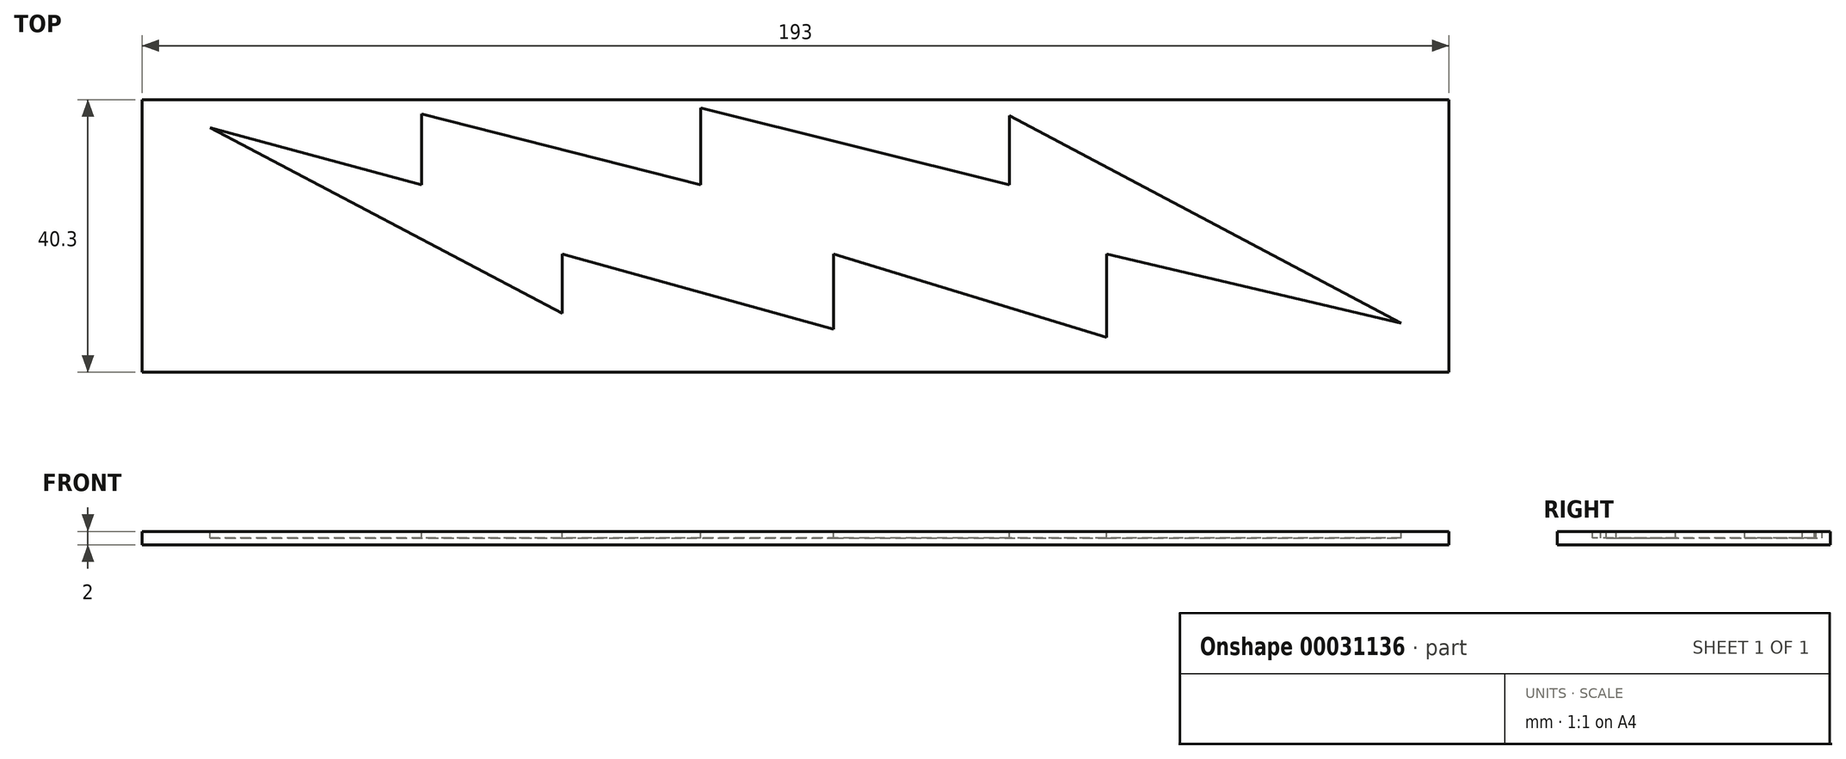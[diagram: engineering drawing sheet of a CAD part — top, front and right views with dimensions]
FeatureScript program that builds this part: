
annotation { "Feature Type Name" : "Feature", "Feature Type Description" : "" }
export const myFeature = defineFeature(function(context is Context, id is Id, definition is map)
    precondition{}
    {
        {
            var Q0;
            Q0=qCreatedBy(makeId("Top.planeOp"),FACE);
            var sketch = newSketch(context, id + "F0", { "sketchPlane" : qUnion([Q0])});
            skLineSegment(sketch, "E0.bottom", {"start": v(-94.67, -12.6) * mm, "end": v(98.33, -12.6) * mm});
            skLineSegment(sketch, "E0.top", {"start": v(-94.67, -52.9) * mm, "end": v(98.33, -52.9) * mm});
            skLineSegment(sketch, "E0.left", {"start": v(-94.67, -12.6) * mm, "end": v(-94.67, -52.9) * mm});
            skLineSegment(sketch, "E0.right", {"start": v(98.33, -12.6) * mm, "end": v(98.33, -52.9) * mm});
            skSolve(sketch);
        }
        {
            var Q0;
            Q0=makeQuery(id+"F0.imprint","IMPRINT",FACE,{"disambiguationData":[TD([[makeQuery(id+"F0.imprint","IMPRINT",EDGE,{"derivedFrom":sQuery(id+"F0.wireOp",EDGE,"E0.bottom")}),-1.0]])]});
            extrude(context, id + "F1", {"entities" : qUnion([Q0]), "depth" : 2 * mm});
        }
        {
            var Q0;
            Q0=makeQuery(id+"F1.opExtrude","CAP_FACE",FACE,{"disambiguationData":[OSD([sQuery(id+"F0.wireOp",EDGE,"E0.bottom"),sQuery(id+"F0.wireOp",EDGE,"E0.top"),sQuery(id+"F0.wireOp",EDGE,"E0.left"),sQuery(id+"F0.wireOp",EDGE,"E0.right")])],"isStart":false});
            var sketch = newSketch(context, id + "F2", { "sketchPlane" : qUnion([Q0])});
            skLineSegment(sketch, "E1", {"start": v(-84.65, -16.74) * mm, "end": v(-32.63, -44.21) * mm});
            skLineSegment(sketch, "E2", {"start": v(-32.63, -44.21) * mm, "end": v(-32.63, -35.44) * mm});
            skLineSegment(sketch, "E3", {"start": v(-32.63, -35.44) * mm, "end": v(7.41, -46.55) * mm});
            skLineSegment(sketch, "E4", {"start": v(7.41, -46.55) * mm, "end": v(7.41, -35.44) * mm});
            skLineSegment(sketch, "E5", {"start": v(7.41, -35.44) * mm, "end": v(47.74, -47.72) * mm});
            skLineSegment(sketch, "E6", {"start": v(47.74, -47.72) * mm, "end": v(47.74, -35.44) * mm});
            skLineSegment(sketch, "E7", {"start": v(47.74, -35.44) * mm, "end": v(91.28, -45.67) * mm});
            skLineSegment(sketch, "E8", {"start": v(91.28, -45.67) * mm, "end": v(33.42, -14.99) * mm});
            skLineSegment(sketch, "E9", {"start": v(33.42, -14.99) * mm, "end": v(33.42, -25.22) * mm});
            skLineSegment(sketch, "E10", {"start": v(33.42, -25.22) * mm, "end": v(-12.17, -13.82) * mm});
            skLineSegment(sketch, "E11", {"start": v(-12.17, -13.82) * mm, "end": v(-12.17, -25.22) * mm});
            skLineSegment(sketch, "E12", {"start": v(-12.17, -25.22) * mm, "end": v(-53.38, -14.7) * mm});
            skLineSegment(sketch, "E13", {"start": v(-53.38, -14.7) * mm, "end": v(-53.38, -25.22) * mm});
            skLineSegment(sketch, "E14", {"start": v(-53.38, -25.22) * mm, "end": v(-84.65, -16.74) * mm});
            skSolve(sketch);
        }
        {
            var Q0;
            Q0=makeQuery(id+"F2.imprint","IMPRINT",FACE,{"disambiguationData":[TD([[makeQuery(id+"F2.imprint","IMPRINT",EDGE,{"derivedFrom":sQuery(id+"F2.wireOp",EDGE,"E1")}),1.0]])]});
            extrude(context, id + "F3", {"entities" : qUnion([Q0]), "operationType" : NewBodyOperationType.REMOVE, "oppositeDirection" : true, "depth" : 1 * mm});
        }
    });
